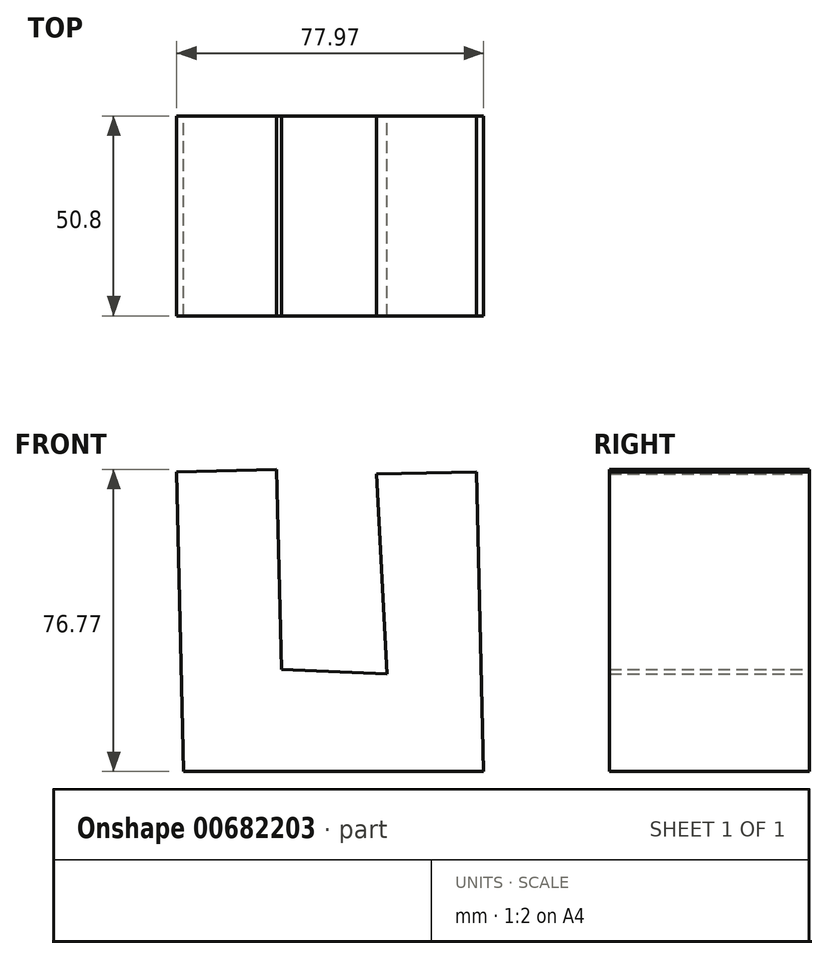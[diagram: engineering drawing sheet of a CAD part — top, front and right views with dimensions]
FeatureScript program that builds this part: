
annotation { "Feature Type Name" : "Feature", "Feature Type Description" : "" }
export const myFeature = defineFeature(function(context is Context, id is Id, definition is map)
    precondition{}
    {
        {
            var Q0;
            Q0=qCreatedBy(makeId("Front.planeOp"),FACE);
            var sketch = newSketch(context, id + "F0", { "sketchPlane" : qUnion([Q0])});
            skLineSegment(sketch, "E0", {"start": v(-42.68, 36.57) * mm, "end": v(-40.9, -39.61) * mm});
            skLineSegment(sketch, "E1", {"start": v(-40.9, -39.61) * mm, "end": v(35.3, -39.61) * mm});
            skLineSegment(sketch, "E2", {"start": v(35.3, -39.61) * mm, "end": v(33.52, 36.57) * mm});
            skLineSegment(sketch, "E3", {"start": v(-42.68, 36.57) * mm, "end": v(-17.29, 37.16) * mm});
            skLineSegment(sketch, "E4", {"start": v(-17.29, 37.16) * mm, "end": v(-16.1, -13.63) * mm});
            skLineSegment(sketch, "E5", {"start": v(33.52, 36.57) * mm, "end": v(8.13, 35.98) * mm});
            skLineSegment(sketch, "E6", {"start": v(8.13, 35.98) * mm, "end": v(10.77, -14.75) * mm});
            skLineSegment(sketch, "E7", {"start": v(-16.1, -13.63) * mm, "end": v(10.77, -14.75) * mm});
            skSolve(sketch);
        }
        {
            var Q0;
            Q0=makeQuery(id+"F0.imprint","IMPRINT",FACE,{"disambiguationData":[TD([[makeQuery(id+"F0.imprint","IMPRINT",EDGE,{"derivedFrom":sQuery(id+"F0.wireOp",EDGE,"E0")}),1.0]])]});
            extrude(context, id + "F1", {"entities" : qUnion([Q0]), "depth" : 50.8 * mm, "offsetDistance" : 25.4 * mm});
        }
    });
